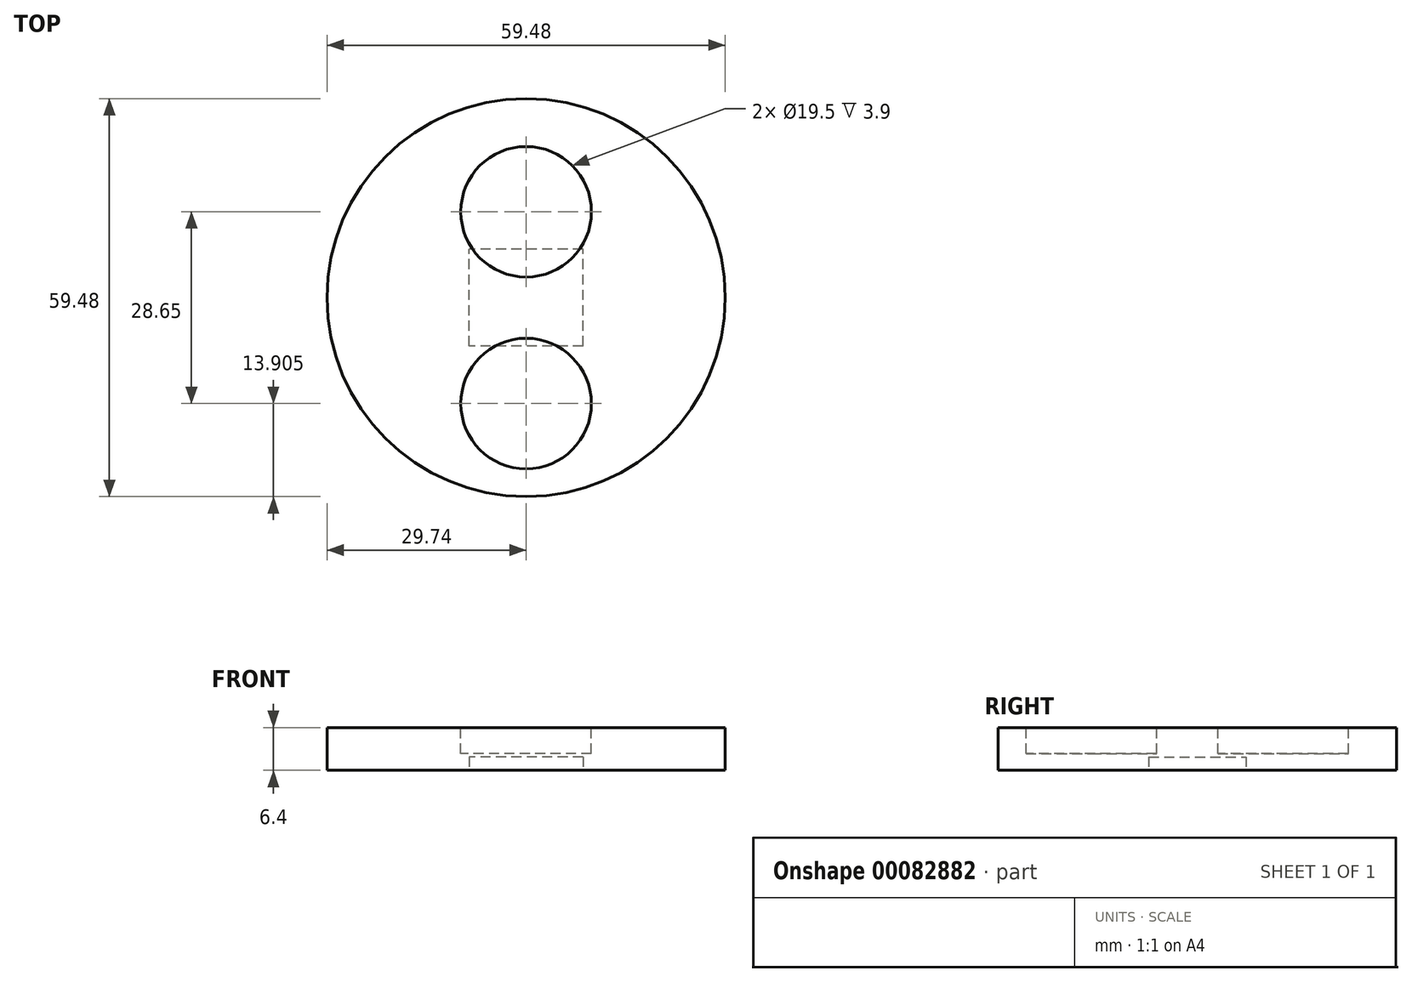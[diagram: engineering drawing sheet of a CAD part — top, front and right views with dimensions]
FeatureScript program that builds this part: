
annotation { "Feature Type Name" : "Feature", "Feature Type Description" : "" }
export const myFeature = defineFeature(function(context is Context, id is Id, definition is map)
    precondition{}
    {
        {
            var Q0;
            Q0=qCreatedBy(makeId("Top.planeOp"),FACE);
            var sketch = newSketch(context, id + "F0", { "sketchPlane" : qUnion([Q0])});
            skCircle(sketch, "E0", {"center": v(0, 0) * mm, "radius": 29.74 * mm});
            skSolve(sketch);
        }
        {
            var Q0;
            Q0=qSketchRegion(id+"F0",true);
            extrude(context, id + "F1", {"entities" : qUnion([Q0]), "depth" : 6.4 * mm});
        }
        {
            var Q0;
            Q0=makeQuery(id+"F1.opExtrude","CAP_FACE",FACE,{"disambiguationData":[OSD([sQuery(id+"F0.wireOp",EDGE,"E0")])],"isStart":false});
            var sketch = newSketch(context, id + "F2", { "sketchPlane" : qUnion([Q0])});
            skCircle(sketch, "E1", {"center": v(0, 12.81) * mm, "radius": 9.75 * mm});
            skCircle(sketch, "E2", {"center": v(0, -15.84) * mm, "radius": 9.75 * mm});
            skSolve(sketch);
        }
        {
            var Q0;
            Q0=qSketchRegion(id+"F2",true);
            extrude(context, id + "F3", {"entities" : qUnion([Q0]), "operationType" : NewBodyOperationType.REMOVE, "oppositeDirection" : true, "depth" : 3.9 * mm});
        }
        {
            var Q0;
            Q0=makeQuery(id+"F1.opExtrude","CAP_FACE",FACE,{"disambiguationData":[OSD([sQuery(id+"F0.wireOp",EDGE,"E0")])],"isStart":true});
            var sketch = newSketch(context, id + "F4", { "sketchPlane" : qUnion([Q0])});
            skLineSegment(sketch, "E3.bottom", {"start": v(8.5, 7.25) * mm, "end": v(-8.5, 7.25) * mm});
            skLineSegment(sketch, "E3.top", {"start": v(8.5, -7.25) * mm, "end": v(-8.5, -7.25) * mm});
            skLineSegment(sketch, "E3.left", {"start": v(8.5, 7.25) * mm, "end": v(8.5, -7.25) * mm});
            skLineSegment(sketch, "E3.right", {"start": v(-8.5, 7.25) * mm, "end": v(-8.5, -7.25) * mm});
            skPoint(sketch, "E3.middle", {"position": v(0, 0) * mm});
            skSolve(sketch);
        }
        {
            var Q0;
            Q0=qSketchRegion(id+"F4",true);
            extrude(context, id + "F5", {"entities" : qUnion([Q0]), "operationType" : NewBodyOperationType.REMOVE, "oppositeDirection" : true, "depth" : 2 * mm});
        }
    });
